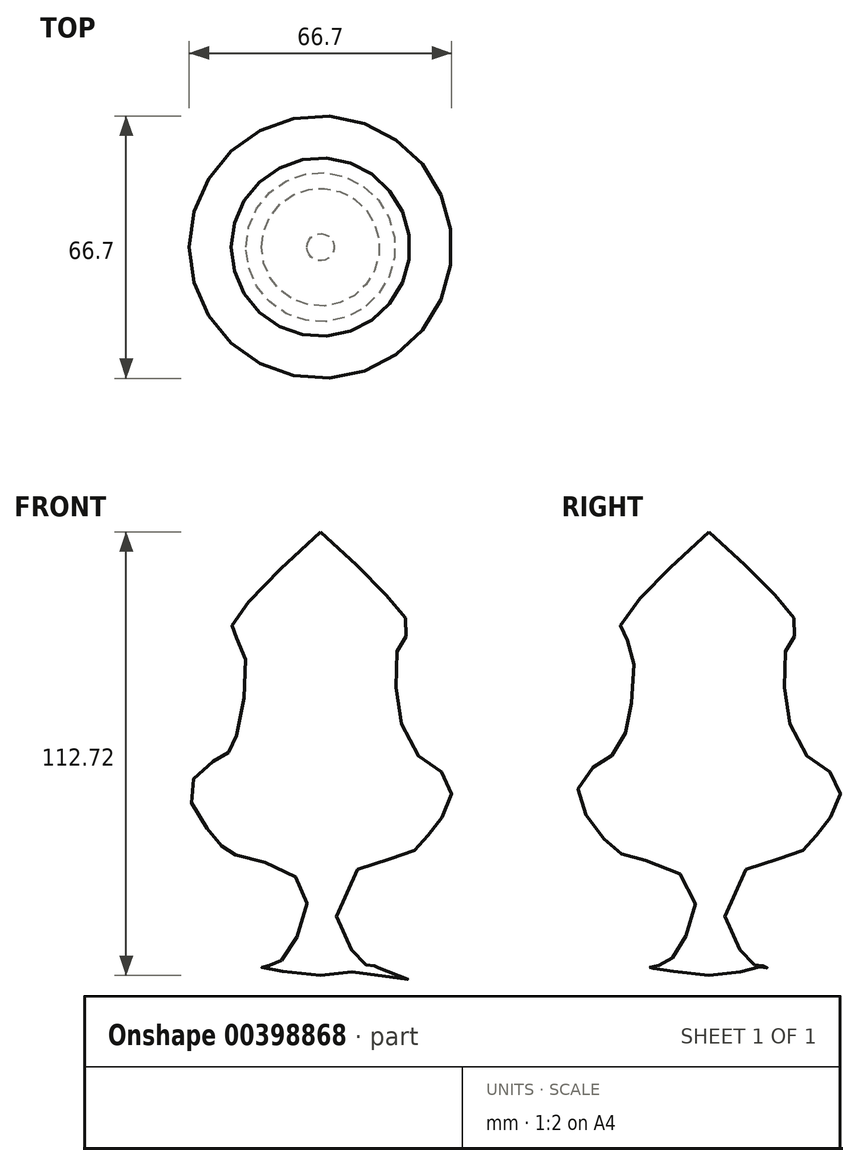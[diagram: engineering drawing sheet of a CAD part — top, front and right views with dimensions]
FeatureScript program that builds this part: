
annotation { "Feature Type Name" : "Feature", "Feature Type Description" : "" }
export const myFeature = defineFeature(function(context is Context, id is Id, definition is map)
    precondition{}
    {
        {
            var Q0;
            Q0=qCreatedBy(makeId("Front.planeOp"),FACE);
            var sketch = newSketch(context, id + "F0", { "sketchPlane" : qUnion([Q0])});
            skLineSegment(sketch, "E0", {"start": v(0, 56.95) * mm, "end": v(0, -55.77) * mm});
            skFitSpline(sketch, "E1", {"points": [v(0, 56.95) * mm, v(-22.66, 32.12) * mm, v(-19.7, 27.59) * mm, v(-22.07, 2.96) * mm, v(-25.03, 0) * mm, v(-33.3, -8.47) * mm, v(-26.21, -21.48) * mm, v(-21.68, -25.03) * mm, v(-4.14, -33.3) * mm, v(-9.66, -51.63) * mm, v(-12.8, -53.2) * mm, v(-14.98, -53.6) * mm, v(0, -55.77) * mm], "startDerivative": vector(-241.49, -221.75) * mm, "endDerivative": vector(238.4, -26.97) * mm});
            skSolve(sketch);
        }
        {
            var Q0;
            Q0=makeQuery(id+"F0.imprint","IMPRINT",FACE,{"disambiguationData":[TD([[makeQuery(id+"F0.imprint","IMPRINT",EDGE,{"derivedFrom":sQuery(id+"F0.wireOp",EDGE,"E0")}),-1.0]])]});
            var Q1;
            Q1=sQuery(id+"F0.wireOp",EDGE,"E0");
            revolve(context, id + "F1", {"entities" : qUnion([Q0]), "axis" : qUnion([Q1]), "revolveType" : RevolveType.FULL});
        }
    });
